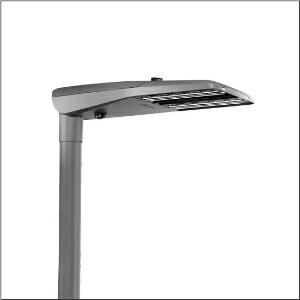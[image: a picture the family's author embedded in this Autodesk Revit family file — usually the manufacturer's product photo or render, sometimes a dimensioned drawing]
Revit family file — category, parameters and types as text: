
# Revit family: streetlight_sl_11_iq_midi___st1_0ab_5xc3n51y08me_91dd
name_source: partatom
category: Lighting Fixtures
units: mm (PartAtom-declared; Revit-internal decimal feet)

## family parameters
Cut with Voids When Loaded = No
Host = Face
Light Source = No
Part Type = Normal
Room Calculation Point = No
Round Connector Dimension = Use Diameter
Shared = No

## types (1)
- --- (1 x LED, 15260 lm, 122.7 W, 3000K)
    Apparent Load = 123 VA
    CIE Flux Codes = 29 63 95 100 100
    Color Rendering = 70
    Color Temperature = 3000K
    Default Elevation = 1800 mm
    Description = Streetlight SL 11 iQ midi, mast luminaire, primary light control with 3 zone facetted reflector, of plastic, silver coated, highly specular, primary optical cover: cover, of PMMA, transparent, light distribution: ST1.0aB, light emission: direct distribution, primary light characteristic: asymmetric, installation type: post-top, side-entry, LED, High Power LED, rated luminous flux: 15.260lm, luminous efficacy: 124lm/W, light colour: 730, colour temperature: 3000K, control: presetting dimming logarithmic, Street-Remote, Auto-Match, Temp-Guard, Lumen-Switch, Night-Set, Smart-Wire, Light-Fading, Desk-Remote (wireless, voltage-free reading and setting of iQ features in the workshop via application-optimized NFC function/RFID function), optimised constant luminous flux control (CLO 2.0), with cable H07RN-F 5x 1.5mm², mains connection: 230..240V, AC, 50/60Hz, connection cable pre-assembled, cable length: 12,5m, start of lifetime: 123W, end of service life: 130W, reduction: 56W, luminaire housing, of diecast aluminium, powder-coated, Siteco® metallic grey (DB 702S), please order mast flange separately, inclination adjustable without tools: 0°, 5°, 10°, 15° (post-top) | 0°, -5°, -10°, -15° (side-entry), sealing non-destructively replaceable, multi-level sealing system, length: 780mm, width: 376mm, height: 118mm, mast flange for spigot size: 42mm (side-entry): 5XC10008XM4, 60/48mm (side-entry/post-top): 5XC10108XM2, 76/60mm (side-entry/post-top): 5XC10108XM1, equipment: Power, Smart Interface below and above, protection rating (complete): IP66, insulation class (complete): insulation class II (safety insulation), certification: CE, ENEC, VDE, UKCA, impact resistance: IK09, permissible operating ambient temperature for outdoor applications: -25..+50°C, standard-compliant lighting for roads and squares, Environmental Product Declaration (EPD) tested and certified by an independent institute, packaging unit: 1 piece

Light Distribution: ST1.0aB
    Height = 118 mm
    Lamp = 1 x LED
    Lamp Light Flux = 15260 lm
    Lamp Power = 122.7 W
    Lamp count = 1
    Length = 780 mm
    Luminous efficacy = 124 lm/W
    Manufacturer = Siteco
    ModVariant = No
    Model = 5XC3N51Y08ME
    Number of Poles = 1
    OnlyDefault = Yes
    Power Factor = 1
    Product Name = Streetlight SL 11 iQ midi | ST1.0aB
    Product group = mast luminaire | pylon top
    ProductGroupID = 6100
    Protection Class = Protection class II
    Protection Degree = IP 66
    RLX_Detail_Level = 1
    RLX_Emergency_Light_Flux = 0 lm
    RLX_Emergency_Type = 0
    RLX_Emergency_Type_DB = No
    RlxData = <blob elided: 69337 chars, md5=6a7073d8>
    Socket = socket
    Standby Power = 0 W
    System Light Flux = 15260 lm
    System Power = 123 W
    Type Comments = factory setting: luminous flux: 100 % | dim-lin: 254 | 552 mA
    Type Image = l_1004429.jpg
    URL = http://relux.com
    VarID = @adj_020069
    Voltage = 0 V
    Weight = 0.00 kg
    Width = 376 mm

## geometry (parser evidence)
native form markers: Blend x4, Sweep x11
no freeform markers — native parametric forms only
